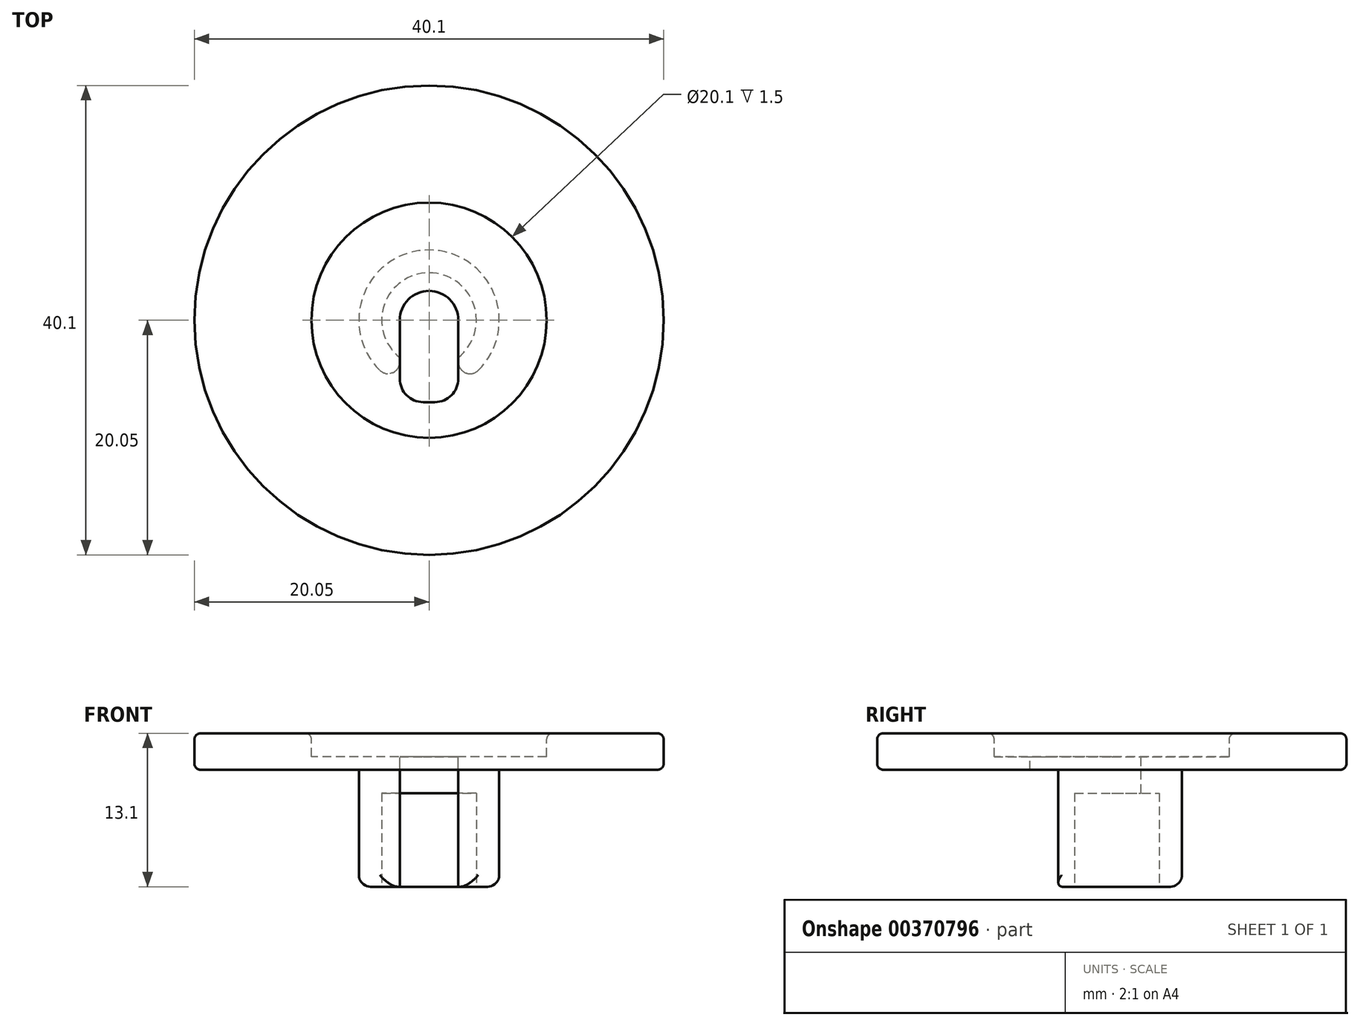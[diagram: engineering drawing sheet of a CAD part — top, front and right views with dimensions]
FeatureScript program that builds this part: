
annotation { "Feature Type Name" : "Feature", "Feature Type Description" : "" }
export const myFeature = defineFeature(function(context is Context, id is Id, definition is map)
    precondition{}
    {
        {
            var Q0;
            Q0=qCreatedBy(makeId("Top.planeOp"),FACE);
            var sketch = newSketch(context, id + "F0", { "sketchPlane" : qUnion([Q0])});
            skCircle(sketch, "E0", {"center": v(0, 0) * mm, "radius": 20.05 * mm});
            skSolve(sketch);
        }
        {
            var Q0;
            Q0 = qSketchRegion(id + "F0", true);
            extrude(context, id + "F1", {"entities" : qUnion([Q0]), "depth" : 3.1 * mm});
        }
        {
            var Q0;
            Q0=makeQuery(id+"F1.opExtrude","CAP_FACE",FACE,{"disambiguationData":[OSD([sQuery(id+"F0.wireOp",EDGE,"E0")])],"isStart":false});
            var sketch = newSketch(context, id + "F2", { "sketchPlane" : qUnion([Q0])});
            skCircle(sketch, "E1", {"center": v(0, 0) * mm, "radius": 10.05 * mm});
            skSolve(sketch);
        }
        {
            var Q0;
            Q0 = qSketchRegion(id + "F2", true);
            extrude(context, id + "F3", {"entities" : qUnion([Q0]), "operationType" : NewBodyOperationType.REMOVE, "oppositeDirection" : true, "depth" : 2 * mm});
        }
        {
            var Q0;
            Q0=makeQuery(id+"F1.opExtrude","CAP_FACE",FACE,{"disambiguationData":[OSD([sQuery(id+"F0.wireOp",EDGE,"E0")])],"isStart":false});
            var Q1;
            Q1=makeQuery(id+"F1.opExtrude","CAP_FACE",FACE,{"disambiguationData":[OSD([sQuery(id+"F0.wireOp",EDGE,"E0")])],"isStart":true});
            fillet(context, id + "F4", {"entities" : qUnion([Q0, Q1]), "radius" : 0.5 * mm, "tangentPropagation" : true, "allowEdgeOverflow" : false});
        }
        {
            var Q0;
            Q0=makeQuery(id+"F1.opExtrude","CAP_FACE",FACE,{"disambiguationData":[OSD([sQuery(id+"F0.wireOp",EDGE,"E0")])],"isStart":true});
            var sketch = newSketch(context, id + "F5", { "sketchPlane" : qUnion([Q0])});
            skArc(sketch, "E2", {"start": v(-2.5, 0) * mm, "mid": v(0, -2.5) * mm, "end": v(2.5, 0) * mm});
            skLineSegment(sketch, "E3.top", {"start": v(-0.5, 7) * mm, "end": v(0.5, 7) * mm});
            skLineSegment(sketch, "E3.left", {"start": v(-2.5, 0) * mm, "end": v(-2.5, 5) * mm});
            skLineSegment(sketch, "E3.right", {"start": v(2.5, 0) * mm, "end": v(2.5, 5) * mm});
            skPoint(sketch, "E4.visualSharp", {"position": v(-2.5, 7) * mm});
            skArc(sketch, "E4.filletArc", {"start": v(-0.5, 7) * mm, "mid": v(-1.91, 6.41) * mm, "end": v(-2.5, 5) * mm});
            skPoint(sketch, "E5.visualSharp", {"position": v(2.5, 7) * mm});
            skArc(sketch, "E5.filletArc", {"start": v(2.5, 5) * mm, "mid": v(1.91, 6.41) * mm, "end": v(0.5, 7) * mm});
            skSolve(sketch);
        }
        {
            var Q0;
            Q0=makeQuery(id+"F1.opExtrude","CAP_FACE",FACE,{"disambiguationData":[OSD([sQuery(id+"F0.wireOp",EDGE,"E0")])],"isStart":true});
            var sketch = newSketch(context, id + "F6", { "sketchPlane" : qUnion([Q0])});
            skCircle(sketch, "E6", {"center": v(0, 0) * mm, "radius": 6 * mm});
            skSolve(sketch);
        }
        {
            var Q0;
            Q0 = qSketchRegion(id + "F6", true);
            extrude(context, id + "F7", {"entities" : qUnion([Q0]), "operationType" : NewBodyOperationType.ADD, "depth" : 10 * mm, "offsetDistance" : 25 * mm});
        }
        {
            var Q0;
            Q0=makeQuery(id+"F7.opExtrude","CAP_FACE",FACE,{"disambiguationData":[OSD([sQuery(id+"F6.wireOp",EDGE,"E6")])],"isStart":false});
            var sketch = newSketch(context, id + "F8", { "sketchPlane" : qUnion([Q0])});
            skCircle(sketch, "E7", {"center": v(0, 0) * mm, "radius": 4.05 * mm});
            skSolve(sketch);
        }
        {
            var Q0;
            Q0 = qSketchRegion(id + "F8", true);
            extrude(context, id + "F9", {"entities" : qUnion([Q0]), "operationType" : NewBodyOperationType.REMOVE, "oppositeDirection" : true, "depth" : 8 * mm, "offsetDistance" : 25 * mm});
        }
        {
            var Q0;
            Q0 = qSketchRegion(id + "F5", true);
            extrude(context, id + "F10", {"entities" : qUnion([Q0]), "operationType" : NewBodyOperationType.REMOVE, "endBound" : BoundingType.THROUGH_ALL, "depth" : 25 * mm, "hasSecondDirection" : true, "secondDirectionBound" : SecondDirectionBoundingType.THROUGH_ALL, "secondDirectionOppositeDirection" : true, "secondDirectionDepth" : 25 * mm, "offsetDistance" : 25 * mm});
        }
        {
            var Q0;
            Q0=makeQuery(id+"F7.opExtrude","CAP_EDGE",EDGE,{"disambiguationData":[OSD([sQuery(id+"F6.wireOp",EDGE,"E6")])],"isStart":false});
            var Q1;
            Q1=makeQuery(id+"F10.boolean.opBoolean","INTERSECT",EDGE,{"derivedFrom":[makeQuery(id+"F7.opExtrude","SWEPT_FACE",FACE,{"disambiguationData":[OSD([sQuery(id+"F6.wireOp",EDGE,"E6")])]}),makeQuery(id+"F10.opExtrude","SWEPT_FACE",FACE,{"disambiguationData":[OSD([sQuery(id+"F5.wireOp",EDGE,"E4.filletArc")])]})]});
            var Q2;
            Q2=makeQuery(id+"F10.boolean.opBoolean","INTERSECT",EDGE,{"derivedFrom":[makeQuery(id+"F7.opExtrude","SWEPT_FACE",FACE,{"disambiguationData":[OSD([sQuery(id+"F6.wireOp",EDGE,"E6")])]}),makeQuery(id+"F10.opExtrude","SWEPT_FACE",FACE,{"disambiguationData":[OSD([sQuery(id+"F5.wireOp",EDGE,"E5.filletArc")])]})]});
            fillet(context, id + "F11", {"entities" : qUnion([Q0, Q1, Q2]), "radius" : 1 * mm, "tangentPropagation" : true, "allowEdgeOverflow" : false});
        }
    });
